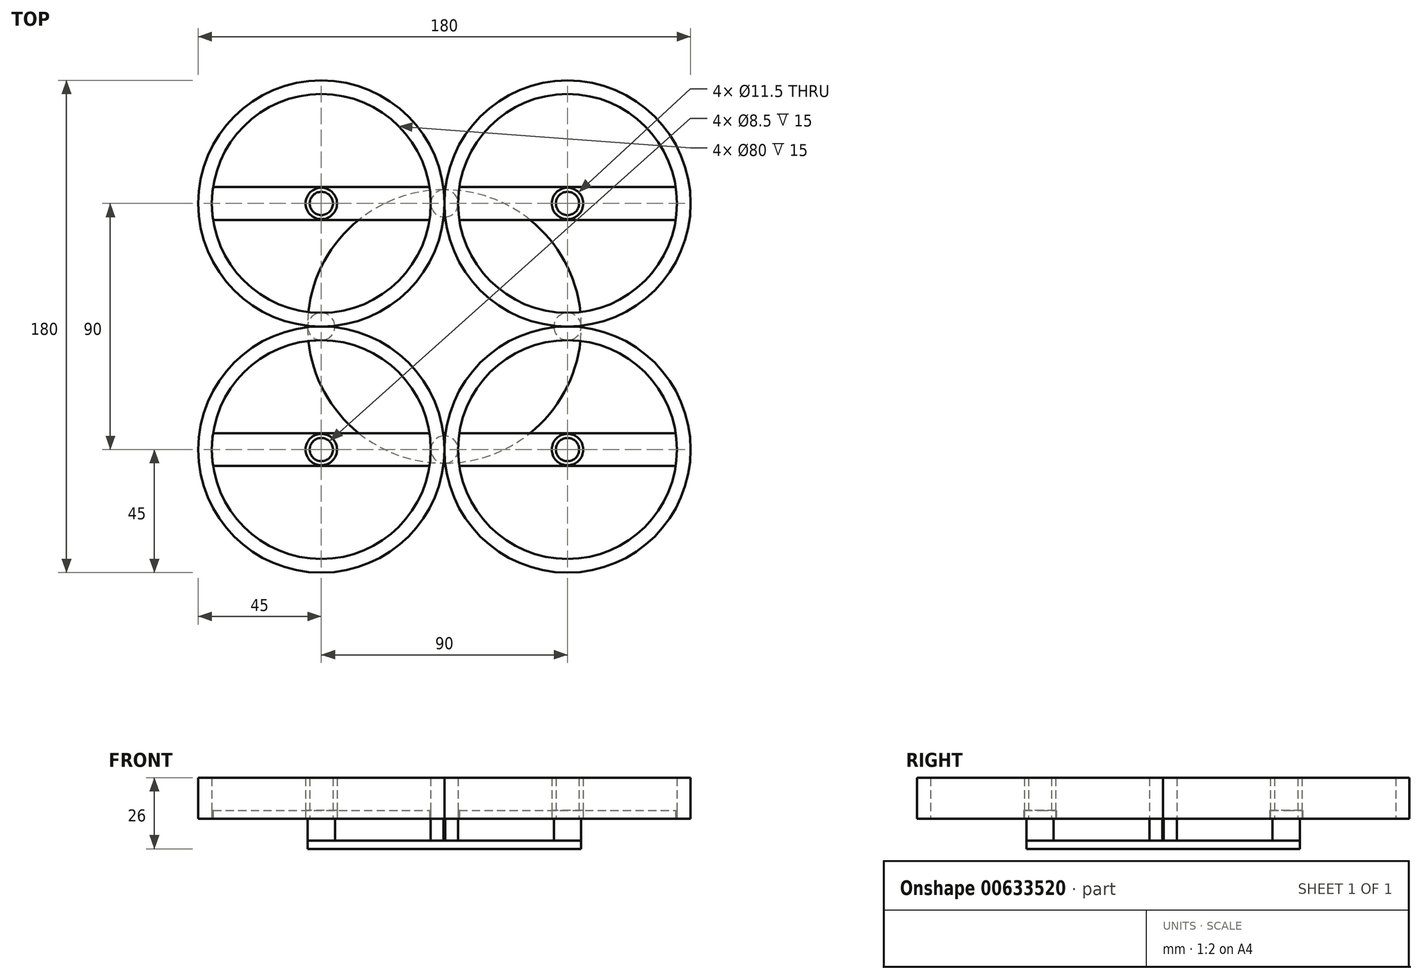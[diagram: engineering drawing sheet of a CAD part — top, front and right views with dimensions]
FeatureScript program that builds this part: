
annotation { "Feature Type Name" : "Feature", "Feature Type Description" : "" }
export const myFeature = defineFeature(function(context is Context, id is Id, definition is map)
    precondition{}
    {
        {
            var Q0;
            Q0=qCreatedBy(makeId("Top.planeOp"),FACE);
            var sketch = newSketch(context, id + "F0", { "sketchPlane" : qUnion([Q0])});
            skLineSegment(sketch, "E0.bottom", {"start": v(-45, 45) * mm, "end": v(45, 45) * mm, "construction": true});
            skLineSegment(sketch, "E0.top", {"start": v(-45, -45) * mm, "end": v(45, -45) * mm, "construction": true});
            skLineSegment(sketch, "E0.left", {"start": v(-45, 45) * mm, "end": v(-45, -45) * mm, "construction": true});
            skLineSegment(sketch, "E0.right", {"start": v(45, 45) * mm, "end": v(45, -45) * mm, "construction": true});
            skPoint(sketch, "E0.middle", {"position": v(0, 0) * mm});
            skCircle(sketch, "E1", {"center": v(-45, 45) * mm, "radius": 45 * mm});
            skCircle(sketch, "E2", {"center": v(45, 45) * mm, "radius": 45 * mm});
            skCircle(sketch, "E3", {"center": v(-45, -45) * mm, "radius": 45 * mm});
            skCircle(sketch, "E4", {"center": v(45, -45) * mm, "radius": 45 * mm});
            skCircle(sketch, "E5", {"center": v(-45, 45) * mm, "radius": 40 * mm});
            skCircle(sketch, "E6", {"center": v(45, 45) * mm, "radius": 40 * mm});
            skCircle(sketch, "E7", {"center": v(-45, -45) * mm, "radius": 40 * mm});
            skCircle(sketch, "E8", {"center": v(45, -45) * mm, "radius": 40 * mm});
            skLineSegment(sketch, "E9", {"start": v(-84.55, 51) * mm, "end": v(-5.45, 51) * mm});
            skLineSegment(sketch, "E10", {"start": v(-84.55, 39) * mm, "end": v(-5.45, 39) * mm});
            skCircle(sketch, "E11", {"center": v(-45, 45) * mm, "radius": 5.75 * mm});
            skCircle(sketch, "E12", {"center": v(-45, 45) * mm, "radius": 4.25 * mm});
            skCircle(sketch, "E13", {"center": v(45, 45) * mm, "radius": 4.25 * mm});
            skCircle(sketch, "E14", {"center": v(45, 45) * mm, "radius": 5.75 * mm});
            skCircle(sketch, "E15", {"center": v(45, -45) * mm, "radius": 4.25 * mm});
            skCircle(sketch, "E16", {"center": v(45, -45) * mm, "radius": 5.75 * mm});
            skCircle(sketch, "E17", {"center": v(-45, -45) * mm, "radius": 5.75 * mm});
            skCircle(sketch, "E18", {"center": v(-45, -45) * mm, "radius": 4.25 * mm});
            skLineSegment(sketch, "E19", {"start": v(5.45, 51) * mm, "end": v(84.55, 51) * mm});
            skLineSegment(sketch, "E20", {"start": v(5.45, 39) * mm, "end": v(84.55, 39) * mm});
            skLineSegment(sketch, "E21", {"start": v(-84.55, -39) * mm, "end": v(-5.45, -39) * mm});
            skLineSegment(sketch, "E22", {"start": v(-84.55, -51) * mm, "end": v(-5.45, -51) * mm});
            skLineSegment(sketch, "E23", {"start": v(5.45, -39) * mm, "end": v(84.55, -39) * mm});
            skLineSegment(sketch, "E24", {"start": v(5.45, -51) * mm, "end": v(84.55, -51) * mm});
            skSolve(sketch);
        }
        {
            var Q0;
            {var subQ6=sQuery(id+"F0.wireOp",EDGE,"E1");var subQ7=makeQuery(id+"F0.imprint","INTERSECT",VERTEX,{"derivedFrom":[subQ6,sQuery(id+"F0.wireOp",EDGE,"E2")]});Q0=makeQuery(id+"F0.imprint","IMPRINT",FACE,{"disambiguationData":[TD([[makeQuery(id+"F0.imprint","IMPRINT",EDGE,{"disambiguationData":[TD([[subQ7,-1.0]])],"derivedFrom":subQ6}),1.0]])]});}
            var Q1;
            {var subQ5=sQuery(id+"F0.wireOp",EDGE,"E2");var subQ6=makeQuery(id+"F0.imprint","INTERSECT",VERTEX,{"derivedFrom":[sQuery(id+"F0.wireOp",EDGE,"E1"),subQ5]});Q1=makeQuery(id+"F0.imprint","IMPRINT",FACE,{"disambiguationData":[TD([[makeQuery(id+"F0.imprint","IMPRINT",EDGE,{"disambiguationData":[TD([[subQ6,-1.0]])],"derivedFrom":subQ5}),1.0]])]});}
            var Q2;
            {var subQ6=sQuery(id+"F0.wireOp",EDGE,"E3");var subQ7=makeQuery(id+"F0.imprint","INTERSECT",VERTEX,{"derivedFrom":[sQuery(id+"F0.wireOp",EDGE,"E1"),subQ6]});Q2=makeQuery(id+"F0.imprint","IMPRINT",FACE,{"disambiguationData":[TD([[makeQuery(id+"F0.imprint","IMPRINT",EDGE,{"disambiguationData":[TD([[subQ7,1.0]])],"derivedFrom":subQ6}),1.0]])]});}
            var Q3;
            {var subQ4=sQuery(id+"F0.wireOp",EDGE,"E4");var subQ5=makeQuery(id+"F0.imprint","INTERSECT",VERTEX,{"derivedFrom":[sQuery(id+"F0.wireOp",EDGE,"E2"),subQ4]});Q3=makeQuery(id+"F0.imprint","IMPRINT",FACE,{"disambiguationData":[TD([[makeQuery(id+"F0.imprint","IMPRINT",EDGE,{"disambiguationData":[TD([[subQ5,-1.0]])],"derivedFrom":subQ4}),1.0]])]});}
            extrude(context, id + "F1", {"entities" : qUnion([Q0, Q1, Q2, Q3]), "depth" : 15 * mm, "offsetDistance" : 25 * mm});
        }
        {
            var Q0;
            Q0=makeQuery(id+"F0.imprint","IMPRINT",FACE,{"disambiguationData":[TD([[makeQuery(id+"F0.imprint","IMPRINT",EDGE,{"derivedFrom":sQuery(id+"F0.wireOp",EDGE,"E16")}),-1.0]])]});
            var Q1;
            Q1=makeQuery(id+"F0.imprint","IMPRINT",FACE,{"disambiguationData":[TD([[makeQuery(id+"F0.imprint","IMPRINT",EDGE,{"derivedFrom":sQuery(id+"F0.wireOp",EDGE,"E14")}),-1.0]])]});
            var Q2;
            {var subQ1=sQuery(id+"F0.wireOp",EDGE,"E9");Q2=makeQuery(id+"F0.imprint","IMPRINT",FACE,{"disambiguationData":[TD([[makeQuery(id+"F0.imprint","IMPRINT",EDGE,{"derivedFrom":subQ1}),-1.0]])]});}
            var Q3;
            Q3=makeQuery(id+"F0.imprint","IMPRINT",FACE,{"disambiguationData":[TD([[makeQuery(id+"F0.imprint","IMPRINT",EDGE,{"derivedFrom":sQuery(id+"F0.wireOp",EDGE,"E17")}),-1.0]])]});
            extrude(context, id + "F2", {"entities" : qUnion([Q0, Q1, Q2, Q3]), "depth" : 3 * mm, "offsetDistance" : 25 * mm});
        }
        {
            var Q0;
            Q0=makeQuery(id+"F0.imprint","IMPRINT",FACE,{"disambiguationData":[TD([[makeQuery(id+"F0.imprint","IMPRINT",EDGE,{"derivedFrom":sQuery(id+"F0.wireOp",EDGE,"E11")}),1.0]])]});
            var Q1;
            Q1=makeQuery(id+"F0.imprint","IMPRINT",FACE,{"disambiguationData":[TD([[makeQuery(id+"F0.imprint","IMPRINT",EDGE,{"derivedFrom":sQuery(id+"F0.wireOp",EDGE,"E13")}),-1.0]])]});
            var Q2;
            Q2=makeQuery(id+"F0.imprint","IMPRINT",FACE,{"disambiguationData":[TD([[makeQuery(id+"F0.imprint","IMPRINT",EDGE,{"derivedFrom":sQuery(id+"F0.wireOp",EDGE,"E17")}),1.0]])]});
            var Q3;
            Q3=makeQuery(id+"F0.imprint","IMPRINT",FACE,{"disambiguationData":[TD([[makeQuery(id+"F0.imprint","IMPRINT",EDGE,{"derivedFrom":sQuery(id+"F0.wireOp",EDGE,"E15")}),-1.0]])]});
            extrude(context, id + "F3", {"entities" : qUnion([Q0, Q1, Q2, Q3]), "depth" : 15 * mm, "offsetDistance" : 25 * mm});
        }
        {
            var Q0;
            Q0=qCreatedBy(makeId("Top.planeOp"),FACE);
            var sketch = newSketch(context, id + "F4", { "sketchPlane" : qUnion([Q0])});
            skCircle(sketch, "E25.0", {"center": v(-45, -45) * mm, "radius": 45 * mm});
            skCircle(sketch, "E26.0", {"center": v(45, -45) * mm, "radius": 45 * mm});
            skCircle(sketch, "E27.0", {"center": v(-45, -45) * mm, "radius": 40 * mm});
            skCircle(sketch, "E28.0", {"center": v(45, -45) * mm, "radius": 40 * mm});
            skCircle(sketch, "E29.0", {"center": v(-45, 45) * mm, "radius": 45 * mm});
            skCircle(sketch, "E30.0", {"center": v(-45, 45) * mm, "radius": 40 * mm});
            skCircle(sketch, "E31.0", {"center": v(45, 45) * mm, "radius": 45 * mm});
            skCircle(sketch, "E32.0", {"center": v(45, 45) * mm, "radius": 40 * mm});
            skCircle(sketch, "E33", {"center": v(0, 45) * mm, "radius": 5 * mm});
            skCircle(sketch, "E34", {"center": v(45, 0) * mm, "radius": 5 * mm});
            skCircle(sketch, "E35", {"center": v(-45, 0) * mm, "radius": 5 * mm});
            skCircle(sketch, "E36", {"center": v(0, -45) * mm, "radius": 5 * mm});
            skSolve(sketch);
        }
        {
            var Q0;
            {var subQ0=sQuery(id+"F4.wireOp",EDGE,"E35");var subQ1=sQuery(id+"F4.wireOp",EDGE,"E29.0");var subQ2=makeQuery(id+"F4.imprint","INTERSECT",VERTEX,{"disambiguationData":[OD(0.0)],"derivedFrom":[subQ1,subQ0]});Q0=makeQuery(id+"F4.imprint","IMPRINT",FACE,{"disambiguationData":[TD([[makeQuery(id+"F4.imprint","IMPRINT",EDGE,{"disambiguationData":[TD([[subQ2,-1.0]])],"derivedFrom":subQ1}),1.0]])]});}
            var Q1;
            {var subQ0=sQuery(id+"F4.wireOp",EDGE,"E35");var subQ1=sQuery(id+"F4.wireOp",EDGE,"E25.0");var subQ2=makeQuery(id+"F4.imprint","INTERSECT",VERTEX,{"disambiguationData":[OD(1.0)],"derivedFrom":[subQ1,subQ0]});Q1=makeQuery(id+"F4.imprint","IMPRINT",FACE,{"disambiguationData":[TD([[makeQuery(id+"F4.imprint","IMPRINT",EDGE,{"disambiguationData":[TD([[subQ2,-1.0]])],"derivedFrom":subQ1}),1.0]])]});}
            var Q2;
            {var subQ0=sQuery(id+"F4.wireOp",EDGE,"E34");var subQ1=sQuery(id+"F4.wireOp",EDGE,"E26.0");var subQ2=makeQuery(id+"F4.imprint","INTERSECT",VERTEX,{"disambiguationData":[OD(0.0)],"derivedFrom":[subQ1,subQ0]});Q2=makeQuery(id+"F4.imprint","IMPRINT",FACE,{"disambiguationData":[TD([[makeQuery(id+"F4.imprint","IMPRINT",EDGE,{"disambiguationData":[TD([[subQ2,-1.0]])],"derivedFrom":subQ1}),1.0]])]});}
            var Q3;
            {var subQ0=sQuery(id+"F4.wireOp",EDGE,"E31.0");var subQ1=makeQuery(id+"F4.imprint","INTERSECT",VERTEX,{"derivedFrom":[sQuery(id+"F4.wireOp",EDGE,"E26.0"),subQ0]});Q3=makeQuery(id+"F4.imprint","IMPRINT",FACE,{"disambiguationData":[TD([[makeQuery(id+"F4.imprint","IMPRINT",EDGE,{"disambiguationData":[TD([[subQ1,1.0]])],"derivedFrom":subQ0}),1.0]])]});}
            var Q4;
            {var subQ0=sQuery(id+"F4.wireOp",EDGE,"E33");var subQ1=sQuery(id+"F4.wireOp",EDGE,"E31.0");var subQ2=makeQuery(id+"F4.imprint","INTERSECT",VERTEX,{"disambiguationData":[OD(0.0)],"derivedFrom":[subQ1,subQ0]});Q4=makeQuery(id+"F4.imprint","IMPRINT",FACE,{"disambiguationData":[TD([[makeQuery(id+"F4.imprint","IMPRINT",EDGE,{"disambiguationData":[TD([[subQ2,-1.0]])],"derivedFrom":subQ1}),1.0]])]});}
            var Q5;
            {var subQ0=sQuery(id+"F4.wireOp",EDGE,"E33");var subQ1=sQuery(id+"F4.wireOp",EDGE,"E29.0");var subQ2=makeQuery(id+"F4.imprint","INTERSECT",VERTEX,{"disambiguationData":[OD(0.0)],"derivedFrom":[subQ1,subQ0]});Q5=makeQuery(id+"F4.imprint","IMPRINT",FACE,{"disambiguationData":[TD([[makeQuery(id+"F4.imprint","IMPRINT",EDGE,{"disambiguationData":[TD([[subQ2,1.0]])],"derivedFrom":subQ1}),1.0]])]});}
            var Q6;
            {var subQ0=sQuery(id+"F4.wireOp",EDGE,"E36");var subQ1=sQuery(id+"F4.wireOp",EDGE,"E25.0");var subQ2=makeQuery(id+"F4.imprint","INTERSECT",VERTEX,{"disambiguationData":[OD(1.0)],"derivedFrom":[subQ1,subQ0]});Q6=makeQuery(id+"F4.imprint","IMPRINT",FACE,{"disambiguationData":[TD([[makeQuery(id+"F4.imprint","IMPRINT",EDGE,{"disambiguationData":[TD([[subQ2,1.0]])],"derivedFrom":subQ1}),1.0]])]});}
            var Q7;
            {var subQ0=sQuery(id+"F4.wireOp",EDGE,"E26.0");var subQ1=makeQuery(id+"F4.imprint","INTERSECT",VERTEX,{"derivedFrom":[sQuery(id+"F4.wireOp",EDGE,"E25.0"),subQ0]});Q7=makeQuery(id+"F4.imprint","IMPRINT",FACE,{"disambiguationData":[TD([[makeQuery(id+"F4.imprint","IMPRINT",EDGE,{"disambiguationData":[TD([[subQ1,1.0]])],"derivedFrom":subQ0}),1.0]])]});}
            extrude(context, id + "F5", {"entities" : qUnion([Q0, Q1, Q2, Q3, Q4, Q5, Q6, Q7]), "oppositeDirection" : true, "depth" : 8 * mm, "offsetDistance" : 25 * mm});
        }
        {
            var Q0;
            Q0=makeQuery(id+"F5.opExtrude","CAP_FACE",FACE,{"disambiguationData":[OSD([sQuery(id+"F4.wireOp",EDGE,"E29.0"),sQuery(id+"F4.wireOp",EDGE,"E35")])],"isStart":false});
            var sketch = newSketch(context, id + "F6", { "sketchPlane" : qUnion([Q0])});
            skCircle(sketch, "E37", {"center": v(0, 0) * mm, "radius": 50 * mm});
            skSolve(sketch);
        }
        {
            var Q0;
            {var subQ0=sQuery(id+"F6.wireOp",EDGE,"E37");var subQ1=sQuery(id+"F4.wireOp",EDGE,"E29.0");var subQ2=makeQuery(id+"F4.imprint","INTERSECT",VERTEX,{"derivedFrom":[sQuery(id+"F4.wireOp",EDGE,"E25.0"),subQ1]});var subQ3=sQuery(id+"F4.wireOp",EDGE,"E35");var subQ5=makeQuery(id+"F4.imprint","INTERSECT",VERTEX,{"disambiguationData":[OD(0.0)],"derivedFrom":[subQ1,subQ3]});var subQ6=makeQuery(id+"F5.opExtrude","CAP_EDGE",EDGE,{"disambiguationData":[OSD([subQ1]),TDD([makeQuery(id+"F4.imprint","IMPRINT",EDGE,{"disambiguationData":[TD([[subQ5,-1.0]])],"derivedFrom":subQ1}),makeQuery(id+"F4.imprint","IMPRINT",EDGE,{"disambiguationData":[TD([[subQ2,-1.0]])],"derivedFrom":subQ1})])],"isStart":false});var subQ7=makeQuery(id+"F6.imprint","INTERSECT",VERTEX,{"derivedFrom":[subQ6,subQ0]});Q0=makeQuery(id+"F6.imprint","IMPRINT",FACE,{"disambiguationData":[TD([[makeQuery(id+"F6.imprint","IMPRINT",EDGE,{"disambiguationData":[TD([[subQ7,1.0]])],"derivedFrom":subQ0}),1.0]])]});}
            var Q1;
            {var subQ0=sQuery(id+"F6.wireOp",EDGE,"E37");var subQ1=sQuery(id+"F4.wireOp",EDGE,"E29.0");var subQ2=makeQuery(id+"F4.imprint","INTERSECT",VERTEX,{"derivedFrom":[sQuery(id+"F4.wireOp",EDGE,"E25.0"),subQ1]});var subQ3=sQuery(id+"F4.wireOp",EDGE,"E35");var subQ5=makeQuery(id+"F4.imprint","INTERSECT",VERTEX,{"disambiguationData":[OD(0.0)],"derivedFrom":[subQ1,subQ3]});var subQ6=makeQuery(id+"F5.opExtrude","CAP_EDGE",EDGE,{"disambiguationData":[OSD([subQ1]),TDD([makeQuery(id+"F4.imprint","IMPRINT",EDGE,{"disambiguationData":[TD([[subQ5,-1.0]])],"derivedFrom":subQ1}),makeQuery(id+"F4.imprint","IMPRINT",EDGE,{"disambiguationData":[TD([[subQ2,-1.0]])],"derivedFrom":subQ1})])],"isStart":false});var subQ7=makeQuery(id+"F6.imprint","INTERSECT",VERTEX,{"derivedFrom":[subQ6,subQ0]});Q1=makeQuery(id+"F6.imprint","IMPRINT",FACE,{"disambiguationData":[TD([[makeQuery(id+"F6.imprint","IMPRINT",EDGE,{"disambiguationData":[TD([[subQ7,-1.0]])],"derivedFrom":subQ0}),1.0]])]});}
            var Q2;
            {var subQ0=sQuery(id+"F4.wireOp",EDGE,"E29.0");var subQ1=makeQuery(id+"F4.imprint","INTERSECT",VERTEX,{"derivedFrom":[sQuery(id+"F4.wireOp",EDGE,"E25.0"),subQ0]});var subQ2=sQuery(id+"F4.wireOp",EDGE,"E35");var subQ4=makeQuery(id+"F4.imprint","INTERSECT",VERTEX,{"disambiguationData":[OD(0.0)],"derivedFrom":[subQ0,subQ2]});Q2=makeQuery(id+"F6.imprint","IMPRINT",FACE,{"disambiguationData":[TD([[makeQuery(id+"F6.imprint","IMPRINT",EDGE,{"derivedFrom":makeQuery(id+"F5.opExtrude","CAP_EDGE",EDGE,{"disambiguationData":[OSD([subQ0]),TDD([makeQuery(id+"F4.imprint","IMPRINT",EDGE,{"disambiguationData":[TD([[subQ4,-1.0]])],"derivedFrom":subQ0}),makeQuery(id+"F4.imprint","IMPRINT",EDGE,{"disambiguationData":[TD([[subQ1,-1.0]])],"derivedFrom":subQ0})])],"isStart":false})}),-1.0]])]});}
            extrude(context, id + "F7", {"entities" : qUnion([Q0, Q1, Q2]), "depth" : 3 * mm, "offsetDistance" : 25 * mm});
        }
    });
